# Revit family: Plumbing-Fixtures_Grohe_Grohtherm_Smart-Control_29124000a
name_source: partatom
category: Plumbing Fixtures
revit_build: Autodesk Revit 2017 (Build: 20190508_0315(x64)
units: mm (PartAtom-declared; Revit-internal decimal feet)

## family parameters
Cut with Voids When Loaded = No
Host = Face
OmniClass Number = 23.45.55.17
OmniClass Title = Mixing Faucets
Part Type = Normal
Room Calculation Point = No
Round Connector Dimension = Use Diameter
Shared = Yes

## types (5) — shared parameters
ADA Compliant = No
Assembly Code = C1030220
AssetType = Fixed
CW Connection = Yes
CWFU = 4.5
ClassificationName = Uniclass 2015
ClassificationValue = Pr_65_54_95_88
Cold Water Connection Diameter = 10 mm  [stored 0.0328084 ft]
Color = Chrome
DurationUnit = Years
Ecojoy = Yes
Finish = Chrome
HW Connection = Yes
HWFU = 4.5
Hot Water Connection Diameter = 10 mm  [stored 0.0328084 ft]
Keynote = N13
Low Emitting Material = No
Manufacturer = Grohe Limited
Masterformat Number = 01 52 19
Masterformat Title = Sanitary Facilities
Material = Chrome
Model = Grohtherm - Smart Control Thermostatic Mixer
NBSDescription = Thermostatic mixing valves
NBSObjectName = Thermostatic mixing valves
NBSReference = 90-10-90/370
ProductionYear = 2016
TypeName = Grohtherm - Smart Control Thermostatic Mixer
URL = www.grohe.com
Vent Connection = No
WarrantyDurationUnit = Years
Waste Connection = No
_current revision = 1
_distributed by = www.bimstore.co.uk
zero-valued in all types: Cost, Default Elevation, ExpectedLife, WFU, _BIMspec_GUID

## per-type parameters (varying)
| type | Faucet Material | ModelNumber | Type Comments |
| 29124000 | Grohe-Chrome-Polished | Grohtherm - 29124000 | Grohtherm - 29124000 |
| 29124A00 | GroheLimited-HardGraphite | Grohtherm - 29124A00 | Grohtherm - 29124A00 |
| 29124AL0 | GroheLimited-BrushedHardGraphite | Grohtherm - 29124AL0 | Grohtherm - 29124AL0 |
| 29124DL0 | GroheLimited-BrushedWarmSunset | Grohtherm - 29124DL0 | Grohtherm - 29124DL0 |
| 29124GN0 | GroheLimited-BrushedCoolSunrise | Grohtherm - 29124GN0 | Grohtherm - 29124GN0 |

note: [stored X ft] marks values corroborated as IEEE doubles in the binary element streams (Revit-internal decimal feet)

## geometry (parser evidence)
native form markers: Blend x8, Sweep x2
no freeform markers — native parametric forms only
